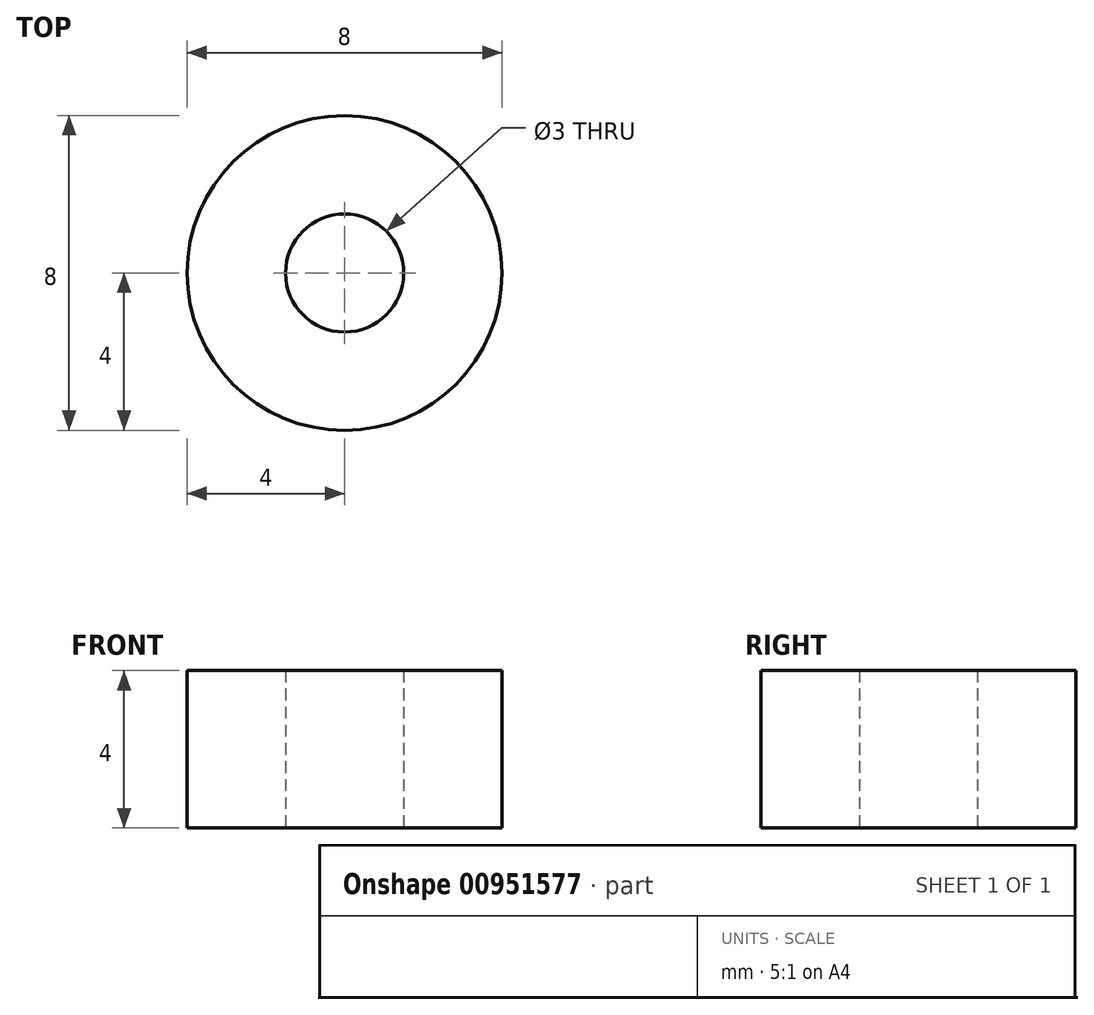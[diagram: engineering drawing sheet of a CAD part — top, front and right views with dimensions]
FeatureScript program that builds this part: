
annotation { "Feature Type Name" : "Feature", "Feature Type Description" : "" }
export const myFeature = defineFeature(function(context is Context, id is Id, definition is map)
    precondition{}
    {
        {
            var Q0;
            Q0=qCreatedBy(makeId("Top.planeOp"),FACE);
            var sketch = newSketch(context, id + "F0", { "sketchPlane" : qUnion([Q0])});
            skCircle(sketch, "E0", {"center": v(0, 0) * mm, "radius": 4 * mm});
            skCircle(sketch, "E1", {"center": v(0, 0) * mm, "radius": 1.5 * mm});
            skSolve(sketch);
        }
        {
            var Q0;
            Q0 = qSketchRegion(id + "F0", true);
            extrude(context, id + "F1", {"entities" : qUnion([Q0]), "depth" : 4 * mm, "offsetDistance" : 25 * mm});
        }
    });
